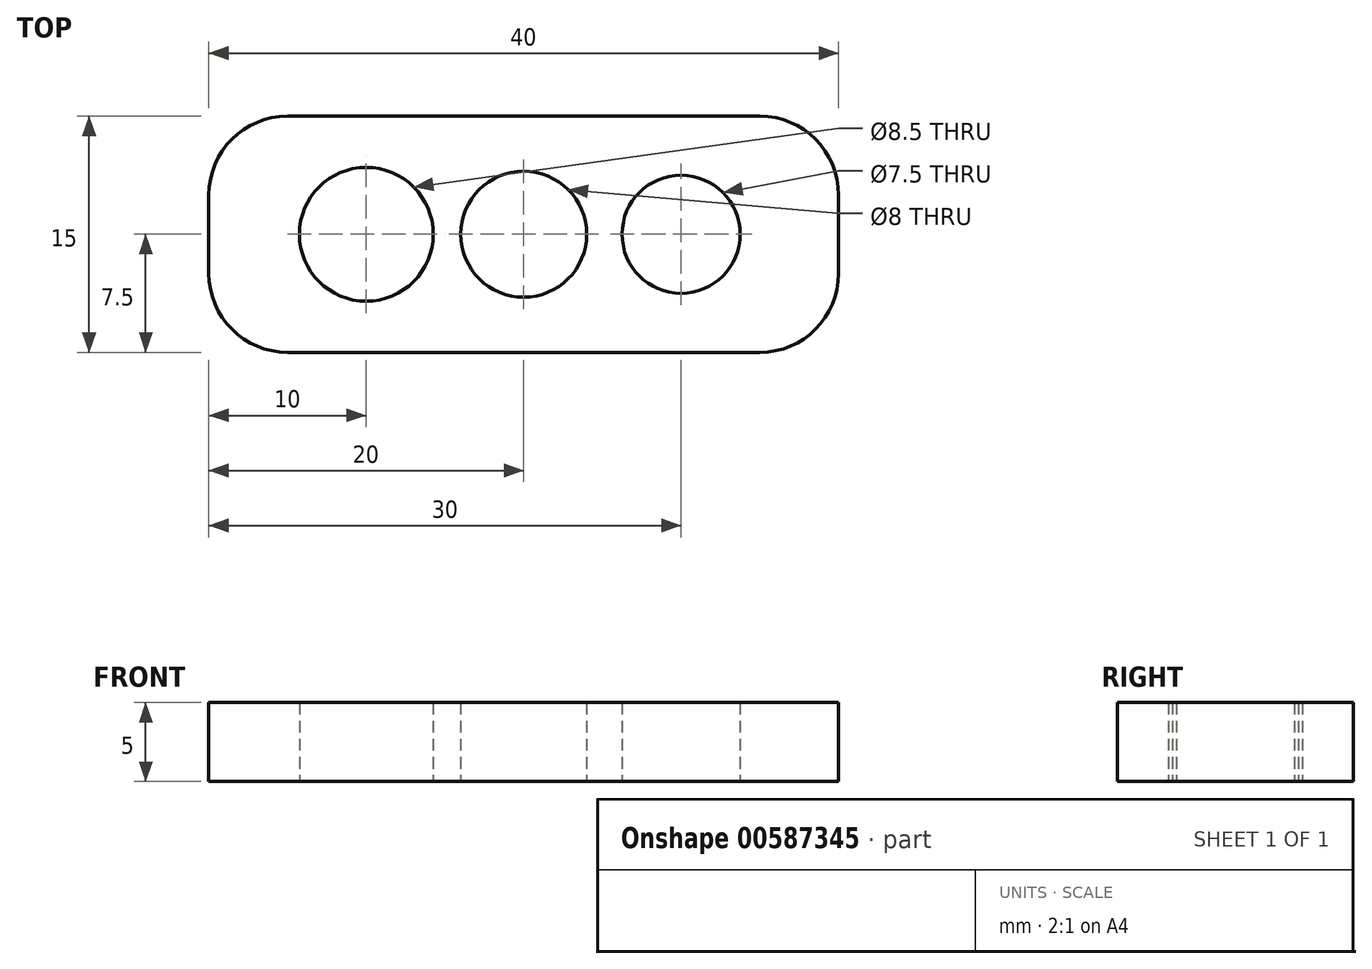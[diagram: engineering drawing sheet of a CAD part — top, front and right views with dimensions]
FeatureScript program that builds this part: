
annotation { "Feature Type Name" : "Feature", "Feature Type Description" : "" }
export const myFeature = defineFeature(function(context is Context, id is Id, definition is map)
    precondition{}
    {
        {
            var Q0;
            Q0=qCreatedBy(makeId("Top.planeOp"),FACE);
            var sketch = newSketch(context, id + "F0", { "sketchPlane" : qUnion([Q0])});
            skLineSegment(sketch, "E0.bottom", {"start": v(-20, 7.5) * mm, "end": v(20, 7.5) * mm});
            skLineSegment(sketch, "E0.top", {"start": v(-20, -7.5) * mm, "end": v(20, -7.5) * mm});
            skLineSegment(sketch, "E0.left", {"start": v(-20, 7.5) * mm, "end": v(-20, -7.5) * mm});
            skLineSegment(sketch, "E0.right", {"start": v(20, 7.5) * mm, "end": v(20, -7.5) * mm});
            skPoint(sketch, "E0.middle", {"position": v(0, 0) * mm});
            skCircle(sketch, "E1", {"center": v(-10, 0) * mm, "radius": 4.25 * mm});
            skCircle(sketch, "E2", {"center": v(10, 0) * mm, "radius": 3.75 * mm});
            skCircle(sketch, "E3", {"center": v(0, 0) * mm, "radius": 4 * mm});
            skSolve(sketch);
        }
        {
            var Q0;
            Q0=makeQuery(id+"F0.imprint","IMPRINT",FACE,{"disambiguationData":[TD([[makeQuery(id+"F0.imprint","IMPRINT",EDGE,{"derivedFrom":sQuery(id+"F0.wireOp",EDGE,"E0.bottom")}),-1.0]])]});
            extrude(context, id + "F1", {"entities" : qUnion([Q0]), "depth" : 5 * mm, "offsetDistance" : 25 * mm});
        }
        {
            var Q0;
            Q0=makeQuery(id+"F1.opExtrude","SWEPT_EDGE",EDGE,{"disambiguationData":[OSD([sQuery(id+"F0.wireOp",EDGE,"E0.bottom"),sQuery(id+"F0.wireOp",EDGE,"E0.left")])]});
            var Q1;
            Q1=makeQuery(id+"F1.opExtrude","SWEPT_EDGE",EDGE,{"disambiguationData":[OSD([sQuery(id+"F0.wireOp",EDGE,"E0.top"),sQuery(id+"F0.wireOp",EDGE,"E0.left")])]});
            var Q2;
            Q2=makeQuery(id+"F1.opExtrude","SWEPT_EDGE",EDGE,{"disambiguationData":[OSD([sQuery(id+"F0.wireOp",EDGE,"E0.bottom"),sQuery(id+"F0.wireOp",EDGE,"E0.right")])]});
            var Q3;
            Q3=makeQuery(id+"F1.opExtrude","SWEPT_EDGE",EDGE,{"disambiguationData":[OSD([sQuery(id+"F0.wireOp",EDGE,"E0.top"),sQuery(id+"F0.wireOp",EDGE,"E0.right")])]});
            fillet(context, id + "F2", {"entities" : qUnion([Q0, Q1, Q2, Q3]), "radius" : 5 * mm, "tangentPropagation" : true, "allowEdgeOverflow" : false});
        }
    });
